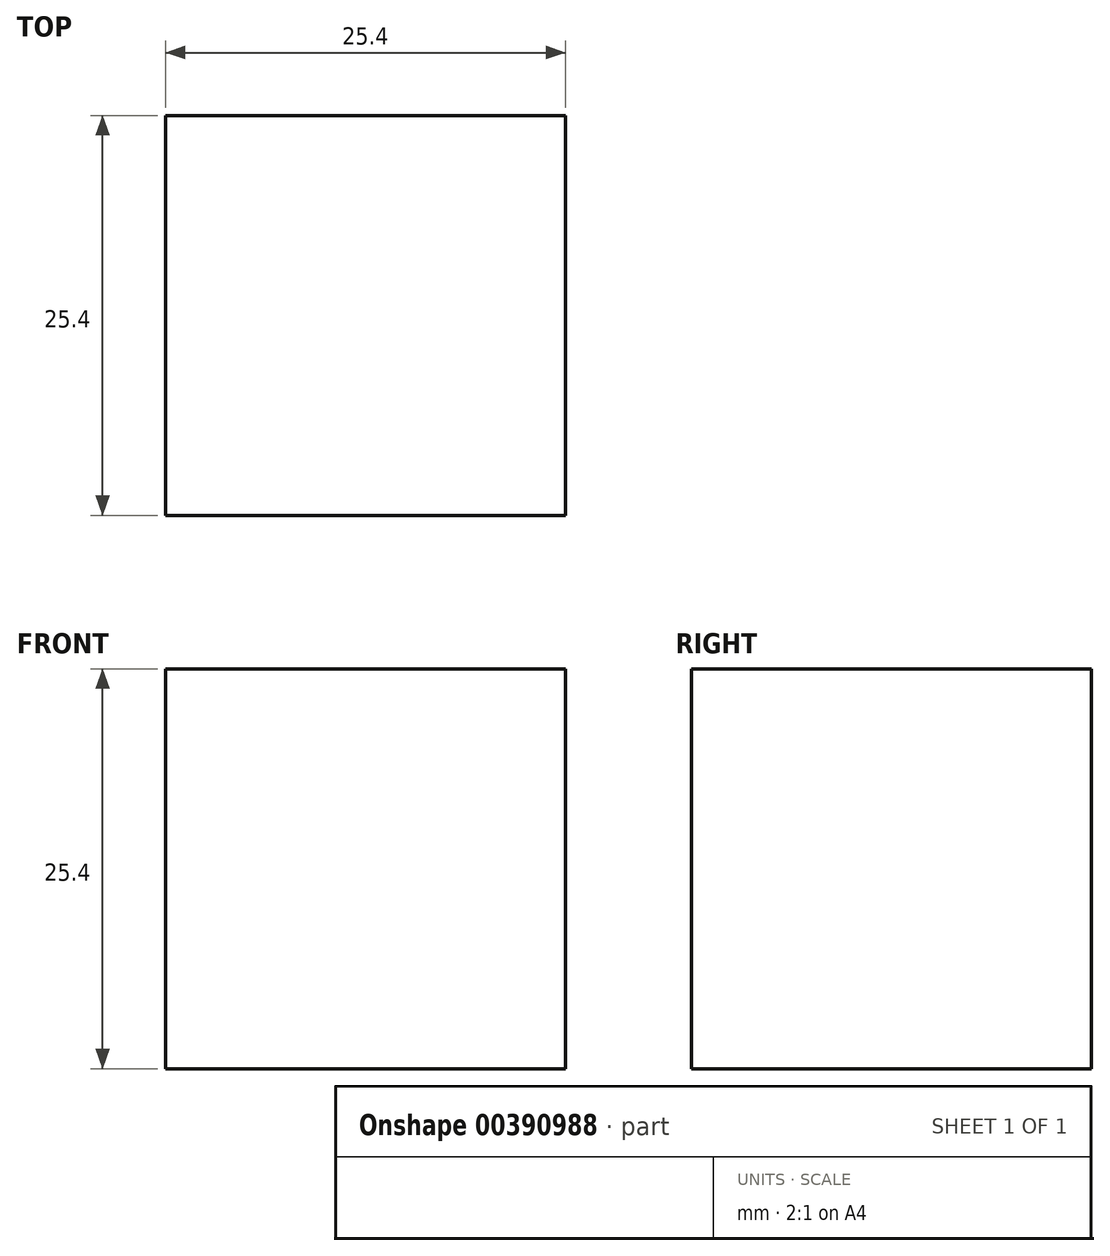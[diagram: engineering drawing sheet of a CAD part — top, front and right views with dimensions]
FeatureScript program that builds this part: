
annotation { "Feature Type Name" : "Feature", "Feature Type Description" : "" }
export const myFeature = defineFeature(function(context is Context, id is Id, definition is map)
    precondition{}
    {
        {
            var Q0;
            Q0=qCreatedBy(makeId("Top.planeOp"),FACE);
            var sketch = newSketch(context, id + "F0", { "sketchPlane" : qUnion([Q0])});
            skLineSegment(sketch, "E0.bottom", {"start": v(-67.9, -11.76) * mm, "end": v(-42.5, -11.76) * mm});
            skLineSegment(sketch, "E0.top", {"start": v(-67.9, -37.16) * mm, "end": v(-42.5, -37.16) * mm});
            skLineSegment(sketch, "E0.left", {"start": v(-67.9, -11.76) * mm, "end": v(-67.9, -37.16) * mm});
            skLineSegment(sketch, "E0.right", {"start": v(-42.5, -11.76) * mm, "end": v(-42.5, -37.16) * mm});
            skSolve(sketch);
        }
        {
            var Q0;
            Q0=makeQuery(id+"F0.imprint","IMPRINT",FACE,{"disambiguationData":[TD([[makeQuery(id+"F0.imprint","IMPRINT",EDGE,{"derivedFrom":sQuery(id+"F0.wireOp",EDGE,"E0.bottom")}),-1.0]])]});
            extrude(context, id + "F1", {"entities" : qUnion([Q0]), "depth" : 25.4 * mm});
        }
    });
